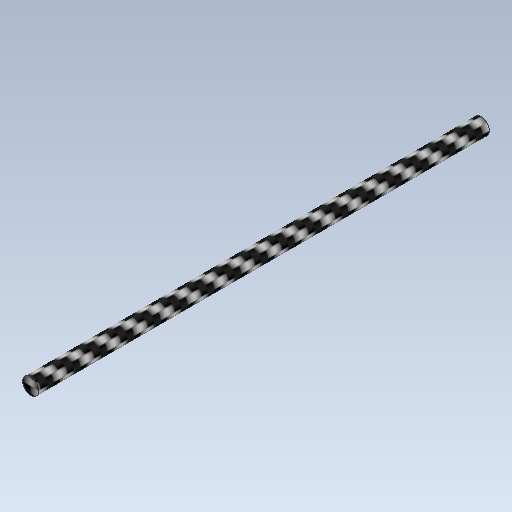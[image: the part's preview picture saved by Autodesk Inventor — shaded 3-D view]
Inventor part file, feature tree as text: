
AUTODESK INVENTOR PART (.ipt)
format: ipt  version: 2020 (Build 240168000, 168)  size: 113,664 bytes
history: native  units: in
note: dims shown in document units (in); Inventor stores cm internally (conversion verified against a paired STEP export)
features: extrude x1, sketch x1
ambient origin geometry x8: Origin, YZ Plane, XZ Plane, XY Plane, X Axis, Y Axis, Z Axis, Center Point
bodies: Solid1 (feature_tree)
feature tree (2):
  extrude  "Extrusion1"  Depth=2.4807in
  sketch  "Sketch1"  dims[d0=0.0906in d1=2.4807in d2=0.0in]
